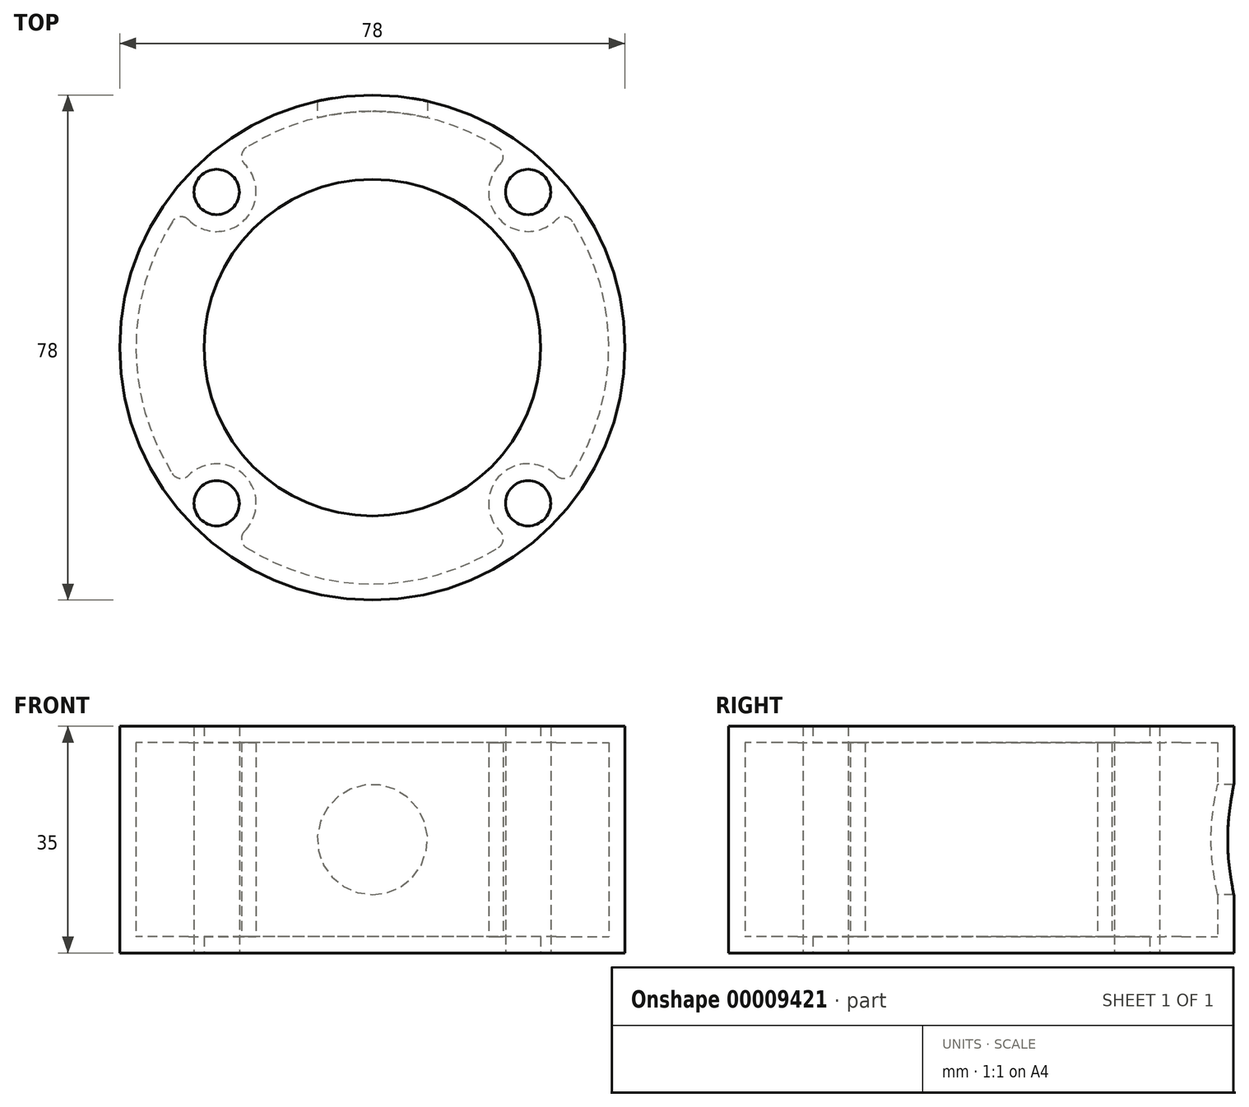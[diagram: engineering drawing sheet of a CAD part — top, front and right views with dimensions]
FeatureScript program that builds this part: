
annotation { "Feature Type Name" : "Feature", "Feature Type Description" : "" }
export const myFeature = defineFeature(function(context is Context, id is Id, definition is map)
    precondition{}
    {
        {
            var Q0;
            Q0=qCreatedBy(makeId("Top.planeOp"),FACE);
            var sketch = newSketch(context, id + "F0", { "sketchPlane" : qUnion([Q0])});
            skCircle(sketch, "E0", {"center": v(0, 0) * mm, "radius": 24 * mm});
            skCircle(sketch, "E1", {"center": v(0, 0) * mm, "radius": 39 * mm});
            skCircle(sketch, "E2", {"center": v(0, 0) * mm, "radius": 3 * mm});
            skCircle(sketch, "E3", {"center": v(0, 0) * mm, "radius": 26 * mm});
            skLineSegment(sketch, "E4", {"start": v(0, 0) * mm, "end": v(-39.55, 39.55) * mm, "construction": true});
            skCircle(sketch, "E5", {"center": v(-24.04, 24.04) * mm, "radius": 3.5 * mm});
            skLineSegment(sketch, "E6", {"start": v(-24.04, 24.04) * mm, "end": v(-17.21, 30.87) * mm, "construction": true});
            skLineSegment(sketch, "E7", {"start": v(-24.04, 24.04) * mm, "end": v(-30, 18.08) * mm, "construction": true});
            skArc(sketch, "E8", {"start": v(-26.59, 21.5) * mm, "mid": v(-21.5, 21.5) * mm, "end": v(-21.5, 26.59) * mm});
            skArc(sketch, "E9", {"start": v(-21.5, 26.59) * mm, "mid": v(-22.68, 29.97) * mm, "end": v(-20.78, 33) * mm});
            skArc(sketch, "E10", {"start": v(-26.59, 21.5) * mm, "mid": v(-29.97, 22.68) * mm, "end": v(-33, 20.78) * mm});
            skLineSegment(sketch, "E11.1.0", {"start": v(-24.04, -24.04) * mm, "end": v(-30.87, -17.21) * mm, "construction": true});
            skArc(sketch, "E11.1.1", {"start": v(-21.5, -26.59) * mm, "mid": v(-21.5, -21.5) * mm, "end": v(-26.59, -21.5) * mm});
            skArc(sketch, "E11.1.2", {"start": v(-21.5, -26.59) * mm, "mid": v(-22.68, -29.97) * mm, "end": v(-20.78, -33) * mm});
            skLineSegment(sketch, "E11.1.3", {"start": v(-24.04, -24.04) * mm, "end": v(-18.08, -30) * mm, "construction": true});
            skArc(sketch, "E11.1.4", {"start": v(-26.59, -21.5) * mm, "mid": v(-29.97, -22.68) * mm, "end": v(-33, -20.78) * mm});
            skCircle(sketch, "E11.1.5", {"center": v(-24.04, -24.04) * mm, "radius": 3.5 * mm});
            skLineSegment(sketch, "E11.2.0", {"start": v(24.04, -24.04) * mm, "end": v(17.21, -30.87) * mm, "construction": true});
            skArc(sketch, "E11.2.1", {"start": v(26.59, -21.5) * mm, "mid": v(21.5, -21.5) * mm, "end": v(21.5, -26.59) * mm});
            skArc(sketch, "E11.2.2", {"start": v(26.59, -21.5) * mm, "mid": v(29.97, -22.68) * mm, "end": v(33, -20.78) * mm});
            skLineSegment(sketch, "E11.2.3", {"start": v(24.04, -24.04) * mm, "end": v(30, -18.08) * mm, "construction": true});
            skArc(sketch, "E11.2.4", {"start": v(21.5, -26.59) * mm, "mid": v(22.68, -29.97) * mm, "end": v(20.78, -33) * mm});
            skCircle(sketch, "E11.2.5", {"center": v(24.04, -24.04) * mm, "radius": 3.5 * mm});
            skLineSegment(sketch, "E11.3.0", {"start": v(24.04, 24.04) * mm, "end": v(30.87, 17.21) * mm, "construction": true});
            skArc(sketch, "E11.3.1", {"start": v(21.5, 26.59) * mm, "mid": v(21.5, 21.5) * mm, "end": v(26.59, 21.5) * mm});
            skArc(sketch, "E11.3.2", {"start": v(21.5, 26.59) * mm, "mid": v(22.68, 29.97) * mm, "end": v(20.78, 33) * mm});
            skLineSegment(sketch, "E11.3.3", {"start": v(24.04, 24.04) * mm, "end": v(18.08, 30) * mm, "construction": true});
            skArc(sketch, "E11.3.4", {"start": v(26.59, 21.5) * mm, "mid": v(29.97, 22.68) * mm, "end": v(33, 20.78) * mm});
            skCircle(sketch, "E11.3.5", {"center": v(24.04, 24.04) * mm, "radius": 3.5 * mm});
            skSolve(sketch);
        }
        {
            var Q0;
            Q0=makeQuery(id+"F0.imprint","IMPRINT",FACE,{"disambiguationData":[TD([[makeQuery(id+"F0.imprint","IMPRINT",EDGE,{"derivedFrom":sQuery(id+"F0.wireOp",EDGE,"E3")}),-1.0]])]});
            extrude(context, id + "F1", {"entities" : qUnion([Q0]), "depth" : 35 * mm});
        }
        {
            var Q0;
            Q0=makeQuery(id+"F0.imprint","IMPRINT",FACE,{"disambiguationData":[TD([[makeQuery(id+"F0.imprint","IMPRINT",EDGE,{"derivedFrom":sQuery(id+"F0.wireOp",EDGE,"E5")}),-1.0]])]});
            var Q1;
            Q1=makeQuery(id+"F0.imprint","IMPRINT",FACE,{"disambiguationData":[TD([[makeQuery(id+"F0.imprint","IMPRINT",EDGE,{"derivedFrom":sQuery(id+"F0.wireOp",EDGE,"E11.3.1")}),1.0]])]});
            var Q2;
            Q2=makeQuery(id+"F0.imprint","IMPRINT",FACE,{"disambiguationData":[TD([[makeQuery(id+"F0.imprint","IMPRINT",EDGE,{"derivedFrom":sQuery(id+"F0.wireOp",EDGE,"E11.2.1")}),1.0]])]});
            var Q3;
            Q3=makeQuery(id+"F0.imprint","IMPRINT",FACE,{"disambiguationData":[TD([[makeQuery(id+"F0.imprint","IMPRINT",EDGE,{"derivedFrom":sQuery(id+"F0.wireOp",EDGE,"E11.1.1")}),1.0]])]});
            extrude(context, id + "F2", {"entities" : qUnion([Q0, Q1, Q2, Q3]), "depth" : 35 * mm});
        }
        {
            var Q0;
            Q0=makeQuery(id+"F1.opExtrude","SWEPT_FACE",FACE,{"disambiguationData":[OSD([sQuery(id+"F0.wireOp",EDGE,"E3")])]});
            shell(context, id + "F3", {"entities" : qUnion([Q0]), "thickness" : 2.5 * mm});
        }
        {
            var Q0;
            Q0=makeQuery(id+"F2.opExtrude","SWEPT_BODY",BODY,{"disambiguationData":[OSD([sQuery(id+"F0.wireOp",EDGE,"E1"),sQuery(id+"F0.wireOp",EDGE,"E5"),sQuery(id+"F0.wireOp",EDGE,"E8"),sQuery(id+"F0.wireOp",EDGE,"E9"),sQuery(id+"F0.wireOp",EDGE,"E10")])]});
            var Q1;
            Q1=makeQuery(id+"F1.opExtrude","SWEPT_BODY",BODY,{"disambiguationData":[OSD([sQuery(id+"F0.wireOp",EDGE,"E1"),sQuery(id+"F0.wireOp",EDGE,"E3"),sQuery(id+"F0.wireOp",EDGE,"E8"),sQuery(id+"F0.wireOp",EDGE,"E9"),sQuery(id+"F0.wireOp",EDGE,"E10"),sQuery(id+"F0.wireOp",EDGE,"E11.1.1"),sQuery(id+"F0.wireOp",EDGE,"E11.1.2"),sQuery(id+"F0.wireOp",EDGE,"E11.1.4"),sQuery(id+"F0.wireOp",EDGE,"E11.2.1"),sQuery(id+"F0.wireOp",EDGE,"E11.2.2"),sQuery(id+"F0.wireOp",EDGE,"E11.2.4"),sQuery(id+"F0.wireOp",EDGE,"E11.3.1"),sQuery(id+"F0.wireOp",EDGE,"E11.3.2"),sQuery(id+"F0.wireOp",EDGE,"E11.3.4")])]});
            var Q2;
            Q2=makeQuery(id+"F2.opExtrude","SWEPT_BODY",BODY,{"disambiguationData":[OSD([sQuery(id+"F0.wireOp",EDGE,"E1"),sQuery(id+"F0.wireOp",EDGE,"E11.2.1"),sQuery(id+"F0.wireOp",EDGE,"E11.2.2"),sQuery(id+"F0.wireOp",EDGE,"E11.2.4"),sQuery(id+"F0.wireOp",EDGE,"E11.2.5")])]});
            var Q3;
            Q3=makeQuery(id+"F2.opExtrude","SWEPT_BODY",BODY,{"disambiguationData":[OSD([sQuery(id+"F0.wireOp",EDGE,"E1"),sQuery(id+"F0.wireOp",EDGE,"E11.3.1"),sQuery(id+"F0.wireOp",EDGE,"E11.3.2"),sQuery(id+"F0.wireOp",EDGE,"E11.3.4"),sQuery(id+"F0.wireOp",EDGE,"E11.3.5")])]});
            var Q4;
            Q4=makeQuery(id+"F2.opExtrude","SWEPT_BODY",BODY,{"disambiguationData":[OSD([sQuery(id+"F0.wireOp",EDGE,"E1"),sQuery(id+"F0.wireOp",EDGE,"E11.1.1"),sQuery(id+"F0.wireOp",EDGE,"E11.1.2"),sQuery(id+"F0.wireOp",EDGE,"E11.1.4"),sQuery(id+"F0.wireOp",EDGE,"E11.1.5")])]});
            booleanBodies(context, id + "F4", {"operationType" : BooleanOperationType.UNION, "tools" : qUnion([Q0, Q1, Q2, Q3, Q4])});
        }
        {
            var Q0;
            Q0=qCreatedBy(makeId("Front.planeOp"),FACE);
            var sketch = newSketch(context, id + "F5", { "sketchPlane" : qUnion([Q0])});
            skCircle(sketch, "E12", {"center": v(0, 17.5) * mm, "radius": 8.5 * mm});
            skSolve(sketch);
        }
        {
            var Q0;
            Q0=makeQuery(id+"F5.imprint","IMPRINT",FACE,{"disambiguationData":[TD([[makeQuery(id+"F5.imprint","IMPRINT",EDGE,{"derivedFrom":sQuery(id+"F5.wireOp",EDGE,"E12")}),1.0]])]});
            extrude(context, id + "F6", {"entities" : qUnion([Q0]), "operationType" : NewBodyOperationType.REMOVE, "oppositeDirection" : true, "depth" : 64.36 * mm});
        }
    });
